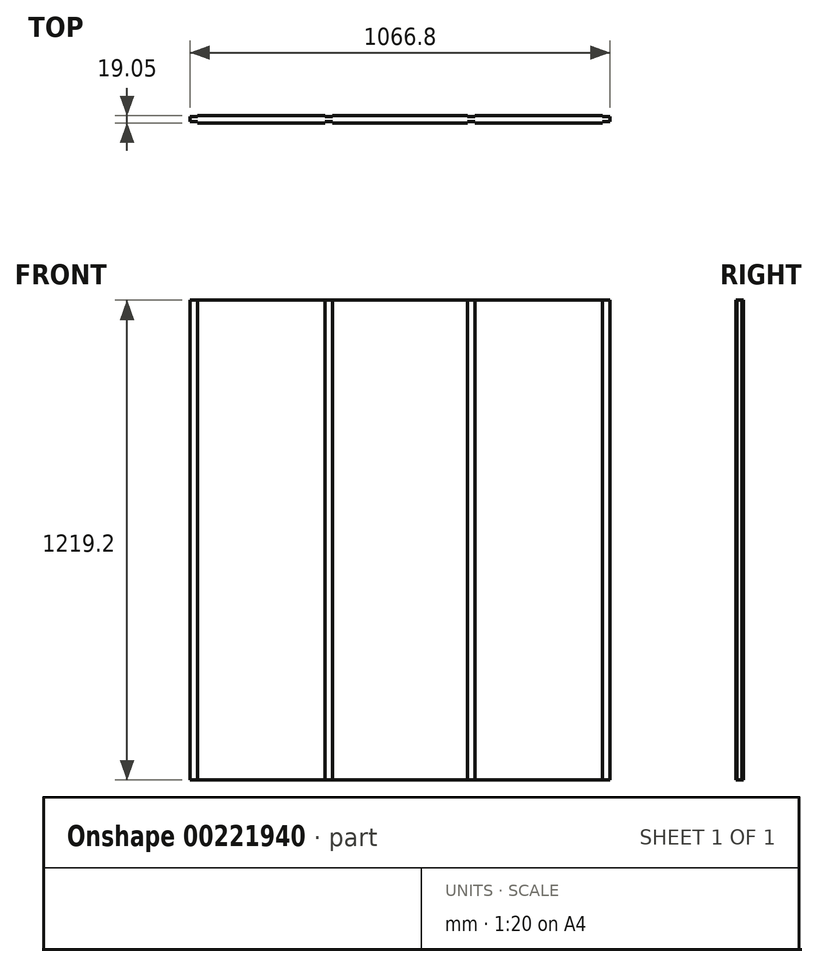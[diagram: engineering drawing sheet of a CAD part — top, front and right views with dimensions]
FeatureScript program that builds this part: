
annotation { "Feature Type Name" : "Feature", "Feature Type Description" : "" }
export const myFeature = defineFeature(function(context is Context, id is Id, definition is map)
    precondition{}
    {
        {
            var Q0;
            Q0=qCreatedBy(makeId("Front.planeOp"),FACE);
            var sketch = newSketch(context, id + "F0", { "sketchPlane" : qUnion([Q0])});
            skLineSegment(sketch, "E0.bottom", {"start": v(-460.61, 767.77) * mm, "end": v(606.19, 767.77) * mm});
            skLineSegment(sketch, "E0.top", {"start": v(-460.61, -451.43) * mm, "end": v(606.19, -451.43) * mm});
            skLineSegment(sketch, "E0.left", {"start": v(-460.61, 767.77) * mm, "end": v(-460.61, -451.43) * mm});
            skLineSegment(sketch, "E0.right", {"start": v(606.19, 767.77) * mm, "end": v(606.19, -451.43) * mm});
            skLineSegment(sketch, "E1.0", {"start": v(263.29, 767.77) * mm, "end": v(263.29, -451.43) * mm});
            skLineSegment(sketch, "E2.0", {"start": v(244.24, 767.77) * mm, "end": v(244.24, -451.43) * mm});
            skLineSegment(sketch, "E3.0", {"start": v(-117.71, 767.77) * mm, "end": v(-117.71, -451.43) * mm});
            skLineSegment(sketch, "E4.0", {"start": v(-98.66, 767.77) * mm, "end": v(-98.66, -451.43) * mm});
            skLineSegment(sketch, "E5.0", {"start": v(-441.56, 767.77) * mm, "end": v(-441.56, -451.43) * mm});
            skLineSegment(sketch, "E6.0", {"start": v(587.14, 767.77) * mm, "end": v(587.14, -451.43) * mm});
            skSolve(sketch);
        }
        {
            var Q0;
            Q0 = qSketchRegion(id + "F0", true);
            extrude(context, id + "F1", {"entities" : qUnion([Q0]), "depth" : 19.05 * mm});
        }
        {
            var Q0;
            {var subQ0=sQuery(id+"F0.wireOp",EDGE,"E0.right");Q0=makeQuery(id+"F0.imprint","IMPRINT",FACE,{"disambiguationData":[TD([[makeQuery(id+"F0.imprint","IMPRINT",EDGE,{"derivedFrom":subQ0}),-1.0]])]});}
            var Q1;
            {var subQ0=sQuery(id+"F0.wireOp",EDGE,"E0.left");Q1=makeQuery(id+"F0.imprint","IMPRINT",FACE,{"disambiguationData":[TD([[makeQuery(id+"F0.imprint","IMPRINT",EDGE,{"derivedFrom":subQ0}),1.0]])]});}
            var Q2;
            {var subQ0=sQuery(id+"F0.wireOp",EDGE,"E1.0");Q2=makeQuery(id+"F0.imprint","IMPRINT",FACE,{"disambiguationData":[TD([[makeQuery(id+"F0.imprint","IMPRINT",EDGE,{"derivedFrom":subQ0}),-1.0]])]});}
            var Q3;
            {var subQ0=sQuery(id+"F0.wireOp",EDGE,"E3.0");Q3=makeQuery(id+"F0.imprint","IMPRINT",FACE,{"disambiguationData":[TD([[makeQuery(id+"F0.imprint","IMPRINT",EDGE,{"derivedFrom":subQ0}),1.0]])]});}
            extrude(context, id + "F2", {"entities" : qUnion([Q0, Q1, Q2, Q3]), "operationType" : NewBodyOperationType.REMOVE, "depth" : 3.17 * mm});
        }
        {
            var Q0;
            Q0=makeQuery(id+"F1.opExtrude","CAP_FACE",FACE,{"disambiguationData":[OSD([sQuery(id+"F0.wireOp",EDGE,"E0.bottom"),sQuery(id+"F0.wireOp",EDGE,"E0.top"),sQuery(id+"F0.wireOp",EDGE,"E0.left"),sQuery(id+"F0.wireOp",EDGE,"E0.right")])],"isStart":false});
            var sketch = newSketch(context, id + "F3", { "sketchPlane" : qUnion([Q0])});
            skLineSegment(sketch, "E7.0", {"start": v(-441.56, 767.77) * mm, "end": v(-441.56, -451.43) * mm});
            skLineSegment(sketch, "E8.0", {"start": v(-117.71, 767.77) * mm, "end": v(-117.71, -451.43) * mm});
            skLineSegment(sketch, "E9.0", {"start": v(-98.66, 767.77) * mm, "end": v(-98.66, -451.43) * mm});
            skLineSegment(sketch, "E10.0", {"start": v(263.29, 767.77) * mm, "end": v(263.29, -451.43) * mm});
            skLineSegment(sketch, "E11.0", {"start": v(244.24, 767.77) * mm, "end": v(244.24, -451.43) * mm});
            skLineSegment(sketch, "E12.0", {"start": v(587.14, 767.77) * mm, "end": v(587.14, -451.43) * mm});
            skSolve(sketch);
        }
        {
            var Q0;
            {var subQ0=sQuery(id+"F3.wireOp",EDGE,"E12.0");Q0=makeQuery(id+"F3.imprint","IMPRINT",FACE,{"disambiguationData":[TD([[makeQuery(id+"F3.imprint","IMPRINT",EDGE,{"derivedFrom":subQ0}),1.0]])]});}
            var Q1;
            {var subQ0=sQuery(id+"F3.wireOp",EDGE,"E7.0");Q1=makeQuery(id+"F3.imprint","IMPRINT",FACE,{"disambiguationData":[TD([[makeQuery(id+"F3.imprint","IMPRINT",EDGE,{"derivedFrom":subQ0}),-1.0]])]});}
            var Q2;
            {var subQ0=sQuery(id+"F3.wireOp",EDGE,"E8.0");Q2=makeQuery(id+"F3.imprint","IMPRINT",FACE,{"disambiguationData":[TD([[makeQuery(id+"F3.imprint","IMPRINT",EDGE,{"derivedFrom":subQ0}),1.0]])]});}
            var Q3;
            {var subQ0=sQuery(id+"F3.wireOp",EDGE,"E10.0");Q3=makeQuery(id+"F3.imprint","IMPRINT",FACE,{"disambiguationData":[TD([[makeQuery(id+"F3.imprint","IMPRINT",EDGE,{"derivedFrom":subQ0}),-1.0]])]});}
            extrude(context, id + "F4", {"entities" : qUnion([Q0, Q1, Q2, Q3]), "operationType" : NewBodyOperationType.REMOVE, "oppositeDirection" : true, "depth" : 3.17 * mm});
        }
    });
